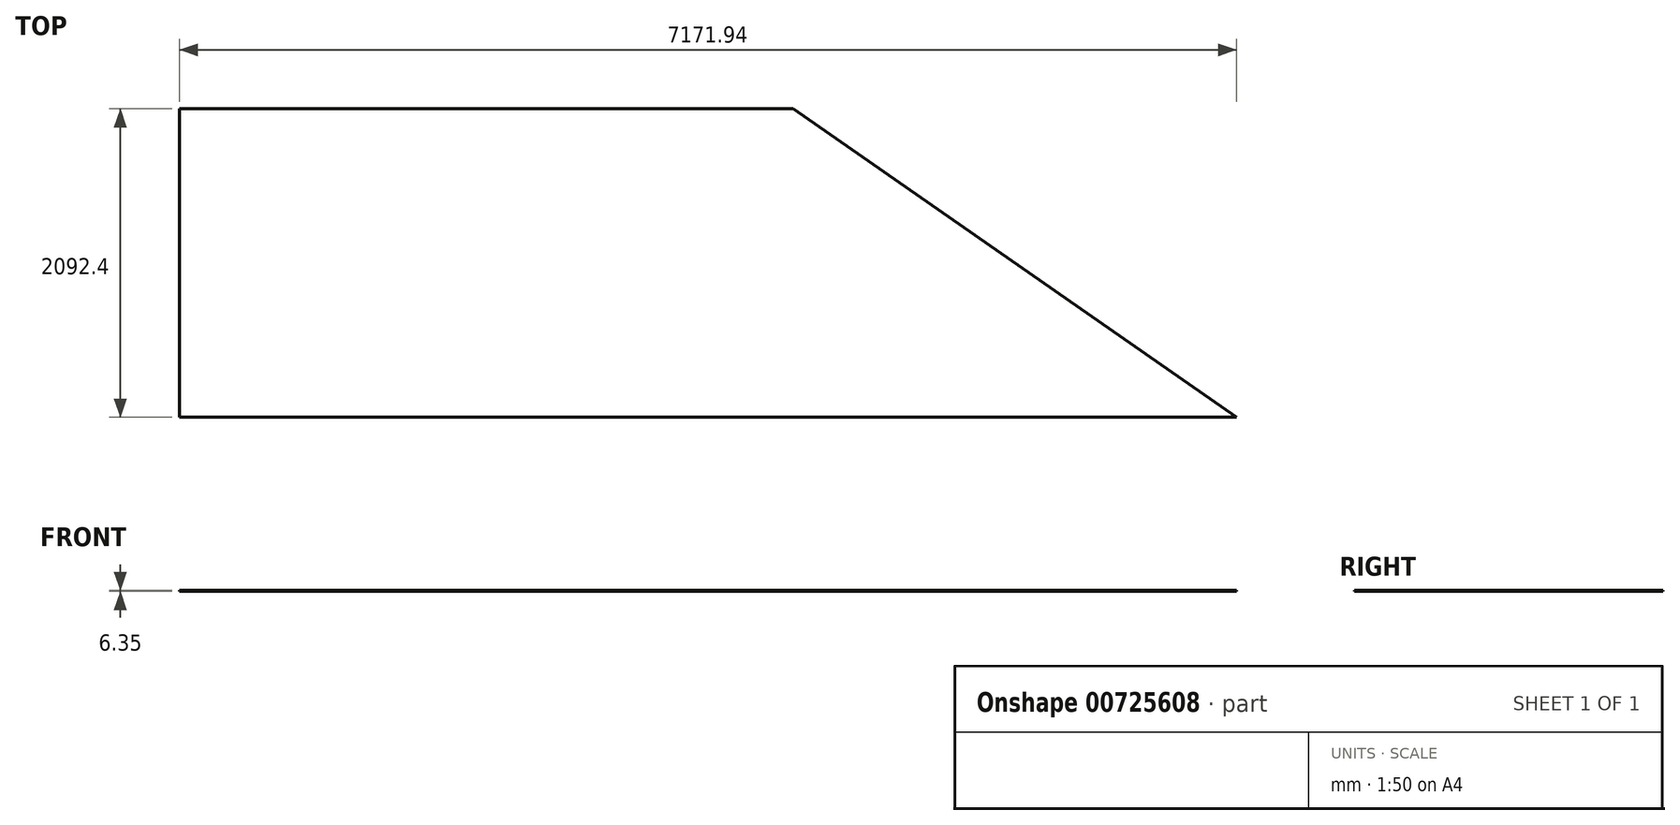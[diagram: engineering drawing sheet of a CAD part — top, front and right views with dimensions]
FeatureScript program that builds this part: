
annotation { "Feature Type Name" : "Feature", "Feature Type Description" : "" }
export const myFeature = defineFeature(function(context is Context, id is Id, definition is map)
    precondition{}
    {
        {
            var Q0;
            Q0=qCreatedBy(makeId("Top.planeOp"),FACE);
            var sketch = newSketch(context, id + "F0", { "sketchPlane" : qUnion([Q0])});
            skLineSegment(sketch, "E0", {"start": v(0, 0) * mm, "end": v(0, 2092.4) * mm});
            skLineSegment(sketch, "E1", {"start": v(0, 2092.4) * mm, "end": v(4163.32, 2092.4) * mm});
            skLineSegment(sketch, "E2", {"start": v(4163.32, 2092.4) * mm, "end": v(7171.94, 0) * mm});
            skLineSegment(sketch, "E3", {"start": v(7171.94, 0) * mm, "end": v(0, 0) * mm});
            skSolve(sketch);
        }
        {
            var Q0;
            Q0 = qSketchRegion(id + "F0", true);
            extrude(context, id + "F1", {"entities" : qUnion([Q0]), "depth" : 6.35 * mm, "offsetDistance" : 25.4 * mm});
        }
    });
